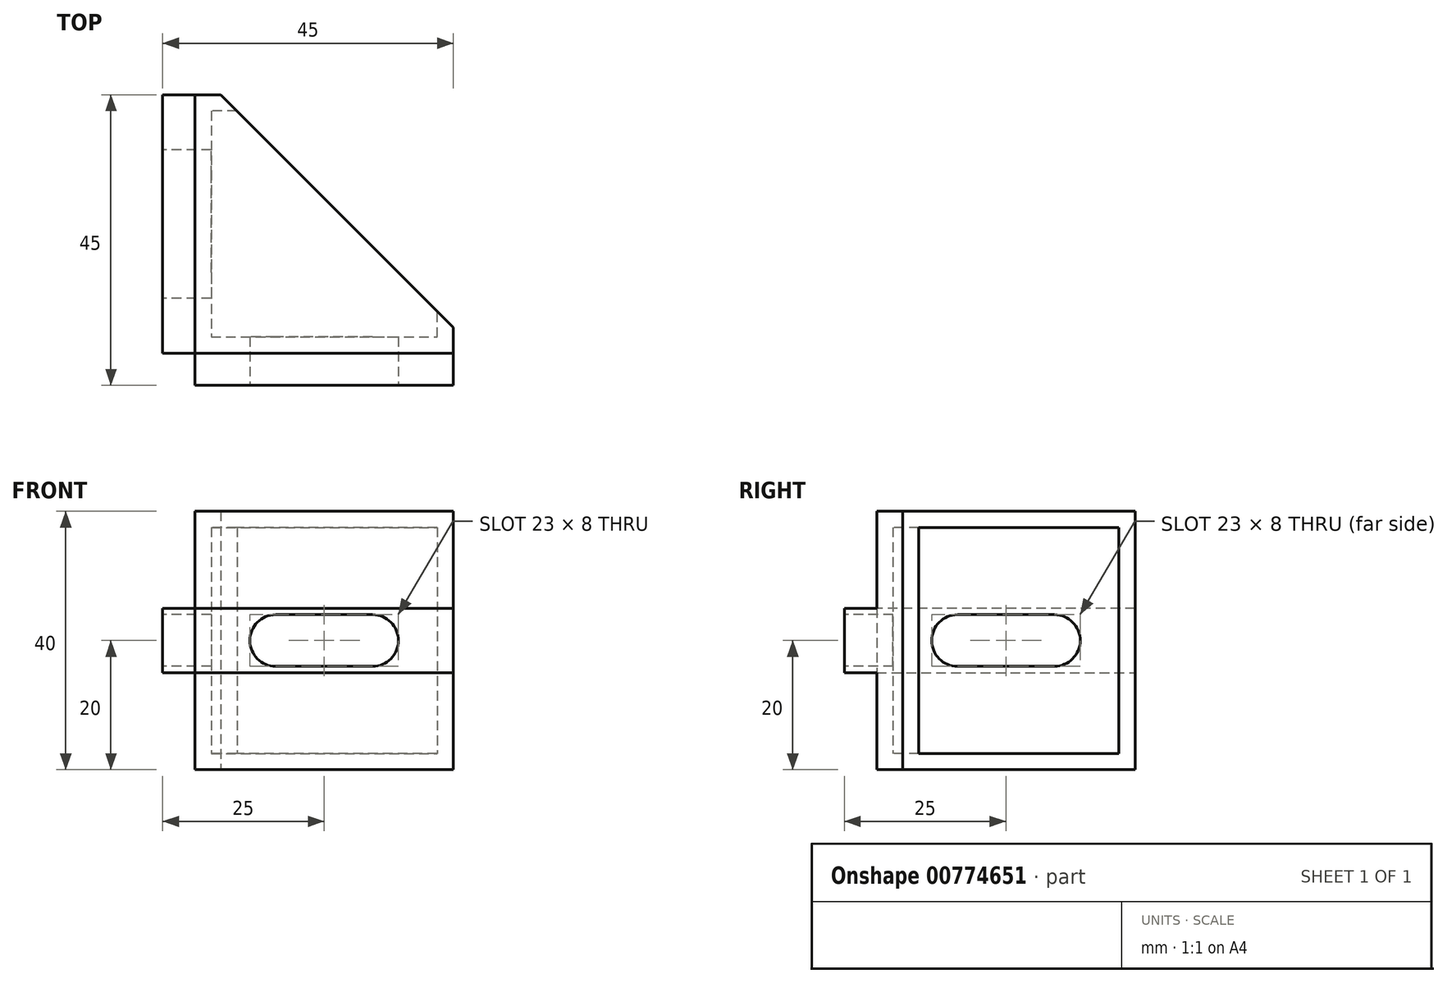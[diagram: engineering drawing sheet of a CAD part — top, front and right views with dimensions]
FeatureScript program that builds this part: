
annotation { "Feature Type Name" : "Feature", "Feature Type Description" : "" }
export const myFeature = defineFeature(function(context is Context, id is Id, definition is map)
    precondition{}
    {
        {
            var Q0;
            Q0=qCreatedBy(makeId("Top.planeOp"),FACE);
            var sketch = newSketch(context, id + "F0", { "sketchPlane" : qUnion([Q0])});
            skLineSegment(sketch, "E0", {"start": v(0, 40) * mm, "end": v(0, 0) * mm});
            skLineSegment(sketch, "E1", {"start": v(0, 0) * mm, "end": v(40, 0) * mm});
            skLineSegment(sketch, "E2", {"start": v(40, 0) * mm, "end": v(40, 4) * mm});
            skLineSegment(sketch, "E3", {"start": v(40, 4) * mm, "end": v(4, 40) * mm});
            skLineSegment(sketch, "E4", {"start": v(4, 40) * mm, "end": v(0, 40) * mm});
            skSolve(sketch);
        }
        {
            var Q0;
            Q0 = qSketchRegion(id + "F0", true);
            extrude(context, id + "F1", {"entities" : qUnion([Q0]), "depth" : 40 * mm, "offsetDistance" : 25 * mm});
        }
        {
            var Q0;
            Q0=makeQuery(id+"F1.opExtrude","SWEPT_FACE",FACE,{"disambiguationData":[OSD([sQuery(id+"F0.wireOp",EDGE,"E3")])]});
            shell(context, id + "F2", {"entities" : qUnion([Q0]), "thickness" : 2.5 * mm});
        }
        {
            var Q0;
            Q0=makeQuery(id+"F1.opExtrude","SWEPT_FACE",FACE,{"disambiguationData":[OSD([sQuery(id+"F0.wireOp",EDGE,"E0")])]});
            var sketch = newSketch(context, id + "F3", { "sketchPlane" : qUnion([Q0])});
            skLineSegment(sketch, "E5", {"start": v(-40, 25) * mm, "end": v(0, 25) * mm});
            skLineSegment(sketch, "E6", {"start": v(0, 25) * mm, "end": v(0, 15) * mm});
            skLineSegment(sketch, "E7", {"start": v(0, 15) * mm, "end": v(-40, 15) * mm});
            skLineSegment(sketch, "E8", {"start": v(-40, 15) * mm, "end": v(-40, 25) * mm});
            skSolve(sketch);
        }
        {
            var Q0;
            Q0 = qSketchRegion(id + "F3", true);
            extrude(context, id + "F4", {"entities" : qUnion([Q0]), "operationType" : NewBodyOperationType.ADD, "depth" : 5 * mm, "offsetDistance" : 25 * mm});
        }
        {
            var Q0;
            Q0=makeQuery(id+"F4.boolean.opBoolean","MERGE",FACE,{"derivedFrom":[makeQuery(id+"F1.opExtrude","SWEPT_FACE",FACE,{"disambiguationData":[OSD([sQuery(id+"F0.wireOp",EDGE,"E1")])]}),makeQuery(id+"F4.opExtrude","SWEPT_FACE",FACE,{"disambiguationData":[OSD([sQuery(id+"F3.wireOp",EDGE,"E6")])]})]});
            var sketch = newSketch(context, id + "F5", { "sketchPlane" : qUnion([Q0])});
            skLineSegment(sketch, "E9.bottom", {"start": v(0, 25) * mm, "end": v(40, 25) * mm});
            skLineSegment(sketch, "E9.top", {"start": v(0, 15) * mm, "end": v(40, 15) * mm});
            skLineSegment(sketch, "E9.left", {"start": v(0, 25) * mm, "end": v(0, 15) * mm});
            skLineSegment(sketch, "E9.right", {"start": v(40, 25) * mm, "end": v(40, 15) * mm});
            skSolve(sketch);
        }
        {
            var Q0;
            Q0 = qSketchRegion(id + "F5", true);
            extrude(context, id + "F6", {"entities" : qUnion([Q0]), "operationType" : NewBodyOperationType.ADD, "depth" : 5 * mm, "offsetDistance" : 25 * mm});
        }
        {
            var Q0;
            Q0=makeQuery(id+"F6.opExtrude","CAP_FACE",FACE,{"disambiguationData":[OSD([sQuery(id+"F5.wireOp",EDGE,"E9.bottom"),sQuery(id+"F5.wireOp",EDGE,"E9.top"),sQuery(id+"F5.wireOp",EDGE,"E9.left"),sQuery(id+"F5.wireOp",EDGE,"E9.right")])],"isStart":false});
            var sketch = newSketch(context, id + "F7", { "sketchPlane" : qUnion([Q0])});
            skArc(sketch, "E10", {"start": v(12.5, 24) * mm, "mid": v(8.5, 20) * mm, "end": v(12.5, 16) * mm});
            skArc(sketch, "E11", {"start": v(27.5, 24) * mm, "mid": v(31.5, 20) * mm, "end": v(27.5, 16) * mm});
            skLineSegment(sketch, "E12", {"start": v(12.5, 16) * mm, "end": v(27.5, 16) * mm});
            skLineSegment(sketch, "E13", {"start": v(27.5, 24) * mm, "end": v(12.5, 24) * mm});
            skSolve(sketch);
        }
        {
            var Q0;
            Q0 = qSketchRegion(id + "F7", true);
            extrude(context, id + "F8", {"entities" : qUnion([Q0]), "operationType" : NewBodyOperationType.REMOVE, "endBound" : BoundingType.THROUGH_ALL, "oppositeDirection" : true, "depth" : 25 * mm, "offsetDistance" : 25 * mm});
        }
        {
            var Q0;
            Q0=makeQuery(id+"F4.opExtrude","CAP_FACE",FACE,{"disambiguationData":[OSD([sQuery(id+"F3.wireOp",EDGE,"E5"),sQuery(id+"F3.wireOp",EDGE,"E6"),sQuery(id+"F3.wireOp",EDGE,"E7"),sQuery(id+"F3.wireOp",EDGE,"E8")])],"isStart":false});
            var sketch = newSketch(context, id + "F9", { "sketchPlane" : qUnion([Q0])});
            skArc(sketch, "E14", {"start": v(-27.5, 16) * mm, "mid": v(-31.5, 20) * mm, "end": v(-27.5, 24) * mm});
            skArc(sketch, "E15", {"start": v(-12.5, 16) * mm, "mid": v(-8.5, 20) * mm, "end": v(-12.5, 24) * mm});
            skLineSegment(sketch, "E16", {"start": v(-27.5, 24) * mm, "end": v(-12.5, 24) * mm});
            skLineSegment(sketch, "E17", {"start": v(-27.5, 16) * mm, "end": v(-12.5, 16) * mm});
            skSolve(sketch);
        }
        {
            var Q0;
            Q0 = qSketchRegion(id + "F9", true);
            extrude(context, id + "F10", {"entities" : qUnion([Q0]), "operationType" : NewBodyOperationType.REMOVE, "endBound" : BoundingType.THROUGH_ALL, "oppositeDirection" : true, "depth" : 25 * mm, "offsetDistance" : 25 * mm});
        }
    });
